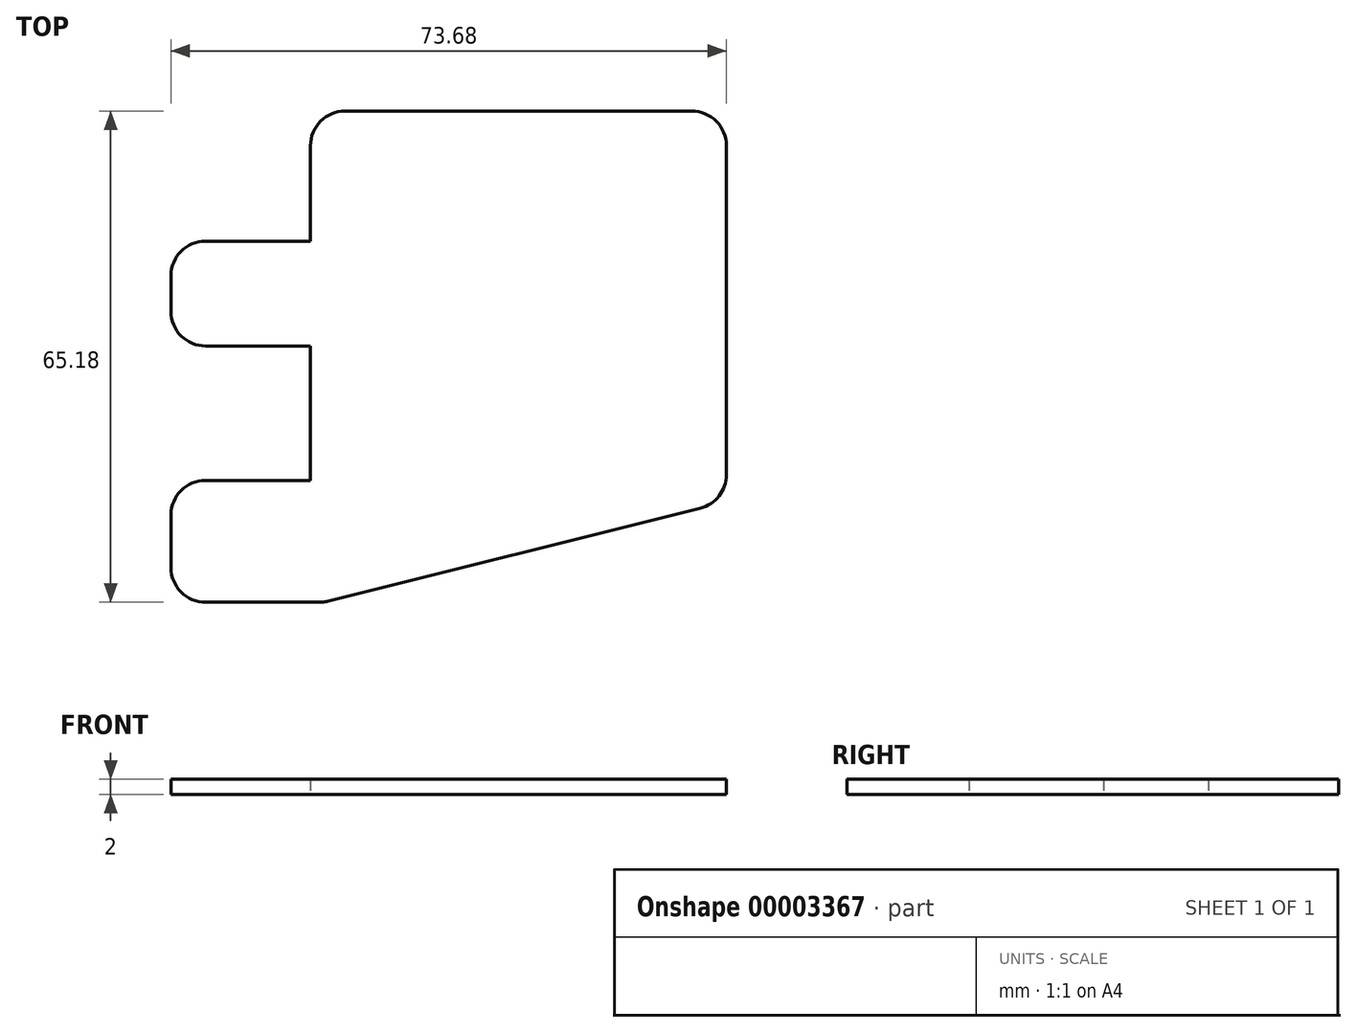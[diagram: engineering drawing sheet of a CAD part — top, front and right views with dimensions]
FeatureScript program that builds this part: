
annotation { "Feature Type Name" : "Feature", "Feature Type Description" : "" }
export const myFeature = defineFeature(function(context is Context, id is Id, definition is map)
    precondition{}
    {
        {
            var Q0;
            Q0=qCreatedBy(makeId("Top.planeOp"),FACE);
            var sketch = newSketch(context, id + "F0", { "sketchPlane" : qUnion([Q0])});
            skLineSegment(sketch, "E0.0", {"start": v(18.13, -1.59) * mm, "end": v(7.5, -1.59) * mm});
            skLineSegment(sketch, "E0.1", {"start": v(7.5, -1.59) * mm, "end": v(3, -1.59) * mm});
            skArc(sketch, "E0.2", {"start": v(-1.59, 3) * mm, "mid": v(-0.24, -0.24) * mm, "end": v(3, -1.59) * mm});
            skLineSegment(sketch, "E0.3", {"start": v(-1.59, 3) * mm, "end": v(-1.59, 10) * mm});
            skArc(sketch, "E0.4", {"start": v(3, 14.59) * mm, "mid": v(-0.24, 13.24) * mm, "end": v(-1.59, 10) * mm});
            skLineSegment(sketch, "E0.5", {"start": v(3, 14.59) * mm, "end": v(7.5, 14.59) * mm});
            skLineSegment(sketch, "E0.6", {"start": v(7.5, 14.59) * mm, "end": v(16.91, 14.59) * mm});
            skLineSegment(sketch, "E0.7", {"start": v(16.91, 14.59) * mm, "end": v(16.91, 32.41) * mm});
            skLineSegment(sketch, "E0.8", {"start": v(7.5, 32.41) * mm, "end": v(16.91, 32.41) * mm});
            skLineSegment(sketch, "E0.9", {"start": v(7.5, 32.41) * mm, "end": v(3, 32.41) * mm});
            skArc(sketch, "E0.10", {"start": v(-1.59, 37) * mm, "mid": v(-0.24, 33.76) * mm, "end": v(3, 32.41) * mm});
            skLineSegment(sketch, "E0.11", {"start": v(-1.59, 37) * mm, "end": v(-1.59, 41.75) * mm});
            skArc(sketch, "E0.12", {"start": v(3, 46.34) * mm, "mid": v(-0.24, 45) * mm, "end": v(-1.59, 41.75) * mm});
            skLineSegment(sketch, "E0.13", {"start": v(3, 46.34) * mm, "end": v(7.5, 46.34) * mm});
            skLineSegment(sketch, "E0.14", {"start": v(7.5, 46.34) * mm, "end": v(16.91, 46.34) * mm});
            skLineSegment(sketch, "E0.15", {"start": v(16.91, 46.34) * mm, "end": v(16.91, 59) * mm});
            skArc(sketch, "E0.16", {"start": v(21.5, 63.59) * mm, "mid": v(18.26, 62.24) * mm, "end": v(16.91, 59) * mm});
            skLineSegment(sketch, "E0.17", {"start": v(21.5, 63.59) * mm, "end": v(67.5, 63.59) * mm});
            skArc(sketch, "E0.18", {"start": v(72.09, 59) * mm, "mid": v(70.74, 62.24) * mm, "end": v(67.5, 63.59) * mm});
            skLineSegment(sketch, "E0.19", {"start": v(72.09, 59) * mm, "end": v(72.09, 15.34) * mm});
            skArc(sketch, "E0.20", {"start": v(68.61, 10.9) * mm, "mid": v(71.12, 12.52) * mm, "end": v(72.09, 15.34) * mm});
            skLineSegment(sketch, "E0.21", {"start": v(68.61, 10.9) * mm, "end": v(19.24, -1.45) * mm});
            skArc(sketch, "E0.22", {"start": v(18.13, -1.59) * mm, "mid": v(18.7, -1.55) * mm, "end": v(19.24, -1.45) * mm});
            skSolve(sketch);
        }
        {
            var Q0;
            Q0=makeQuery(id+"F0.imprint","IMPRINT",FACE,{"disambiguationData":[TD([[makeQuery(id+"F0.imprint","IMPRINT",EDGE,{"derivedFrom":sQuery(id+"F0.wireOp",EDGE,"E0.0")}),-1.0]])]});
            extrude(context, id + "F1", {"entities" : qUnion([Q0]), "depth" : 2 * mm});
        }
    });
